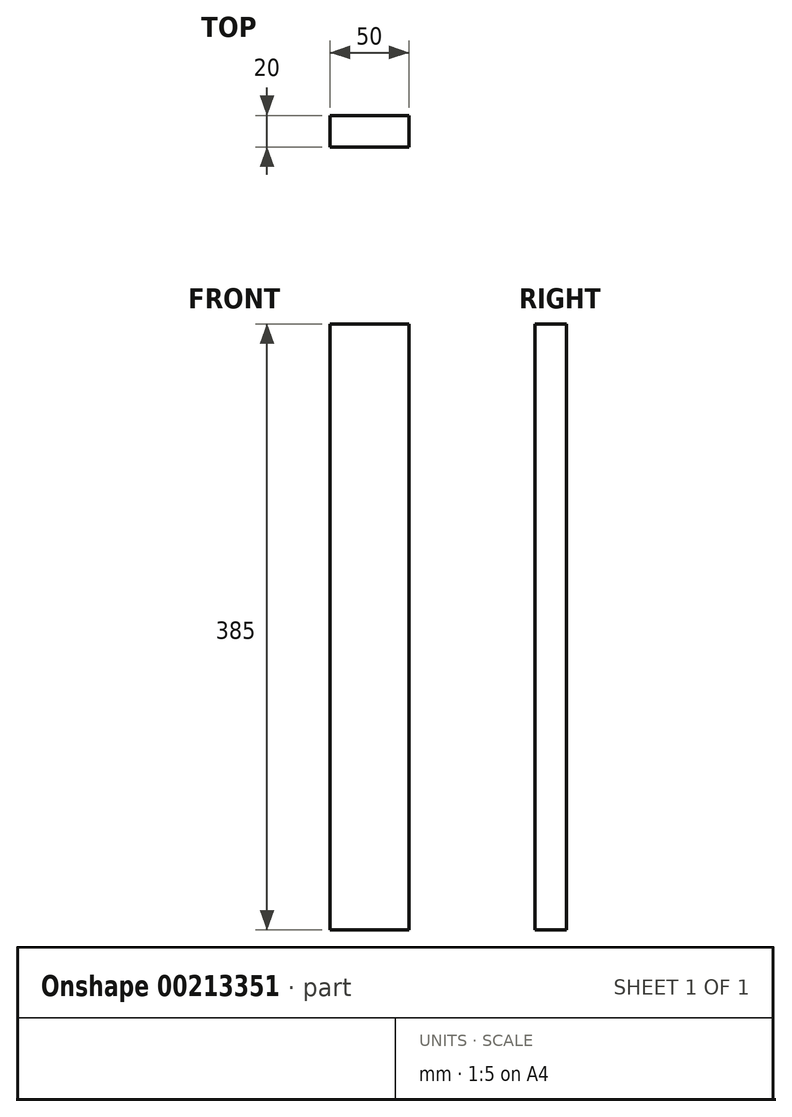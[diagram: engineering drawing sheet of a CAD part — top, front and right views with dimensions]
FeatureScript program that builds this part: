
annotation { "Feature Type Name" : "Feature", "Feature Type Description" : "" }
export const myFeature = defineFeature(function(context is Context, id is Id, definition is map)
    precondition{}
    {
        {
            var Q0;
            Q0=qCreatedBy(makeId("Front.planeOp"),FACE);
            var sketch = newSketch(context, id + "F0", { "sketchPlane" : qUnion([Q0])});
            skLineSegment(sketch, "E0.bottom", {"start": v(25, 192.5) * mm, "end": v(-25, 192.5) * mm});
            skLineSegment(sketch, "E0.top", {"start": v(25, -192.5) * mm, "end": v(-25, -192.5) * mm});
            skLineSegment(sketch, "E0.left", {"start": v(25, 192.5) * mm, "end": v(25, -192.5) * mm});
            skLineSegment(sketch, "E0.right", {"start": v(-25, 192.5) * mm, "end": v(-25, -192.5) * mm});
            skPoint(sketch, "E0.middle", {"position": v(0, 0) * mm});
            skSolve(sketch);
        }
        {
            var Q0;
            Q0=makeQuery(id+"F0.imprint","IMPRINT",FACE,{"disambiguationData":[TD([[makeQuery(id+"F0.imprint","IMPRINT",EDGE,{"derivedFrom":sQuery(id+"F0.wireOp",EDGE,"E0.bottom")}),1.0]])]});
            extrude(context, id + "F1", {"entities" : qUnion([Q0]), "depth" : 20 * mm});
        }
    });
